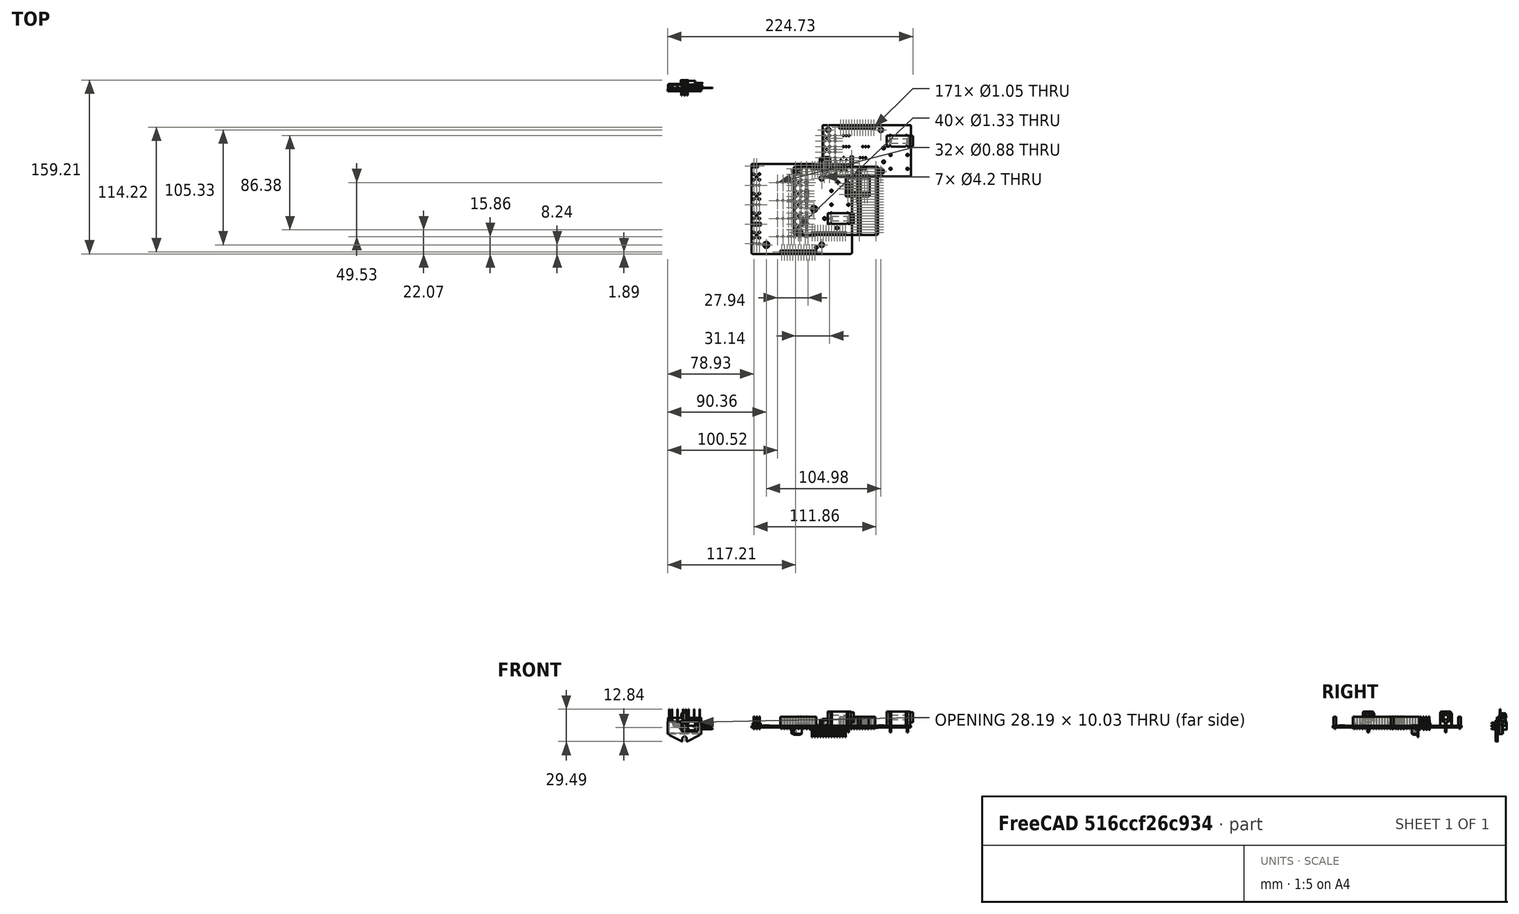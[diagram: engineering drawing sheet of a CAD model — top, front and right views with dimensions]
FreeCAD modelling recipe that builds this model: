
FCSTD DOCUMENT  (FreeCAD 1.1R20260108 (Git shallow))
Label: KiCadStepUp
License: All rights reserved
LicenseURL: https://en.wikipedia.org/wiki/All_rights_reserved
objects: Part::Feature×96, App::Link×57, App::Point×27, App::Part×27, PartDesign::CoordinateSystem×4, Sketcher::SketchObject×4
note: 108 computed .brp shape members not serialized (recipe doc carries the construction recipe); baked Part::Feature solids carry a one-line shape summary decoded from their .brp

FEATURE [App::Point] Origin028  label="Origin038"
  Role = Origin
FEATURE [PartDesign::CoordinateSystem] Local_CS_ba79
  AttacherType = Attacher::AttachEngine3D
  MapMode = 2
FEATURE [App::Point] Origin030
  Role = Origin
FEATURE [Part::Feature] Pcb_ba79
  shape: bbox 76.99 x 62.48 x 1.857 mm, 142 faces (baked)
FEATURE [Sketcher::SketchObject] PCB_Sketch_ba79
  ArcFitTolerance = 1e-06
  ExternalTypes = [0]
  FullyConstrained = false
  MakeInternals = false
  sketch-geometry (8):
    g0: LineSegment StartX=100.265 StartY=-130.75 StartZ=0 EndX=100.265 EndY=-70.27 EndZ=0
    g1: LineSegment StartX=176.25 StartY=-131.75 StartZ=0 EndX=101.265 EndY=-131.75 EndZ=0
    g2: LineSegment StartX=177.25 StartY=-70.27 StartZ=0 EndX=177.25 EndY=-130.75 EndZ=0
    g3: LineSegment StartX=101.265 StartY=-69.27 StartZ=0 EndX=176.25 EndY=-69.27 EndZ=0
    g4: ArcOfCircle CenterX=101.265 CenterY=-130.75 CenterZ=0 NormalX=0 NormalY=0 NormalZ=-1 AngleXU=-1.5708 Radius=0.999999 StartAngle=0 EndAngle=1.5708
    g5: ArcOfCircle CenterX=176.25 CenterY=-70.27 CenterZ=0 NormalX=0 NormalY=0 NormalZ=-1 AngleXU=1.5708 Radius=0.999999 StartAngle=0 EndAngle=1.5708
    g6: ArcOfCircle CenterX=176.25 CenterY=-130.75 CenterZ=0 NormalX=0 NormalY=0 NormalZ=-1 AngleXU=3.14159 Radius=0.999999 StartAngle=0 EndAngle=1.5708
    g7: ArcOfCircle CenterX=101.265 CenterY=-70.27 CenterZ=0 NormalX=0 NormalY=0 NormalZ=-1 AngleXU=-7.47076e-07 Radius=0.999999 StartAngle=0 EndAngle=1.5708
  constraints (8):
    c: Coincident(g0,g4)
    c: Coincident(g0,g7)
    c: Coincident(g1,g4)
    c: Coincident(g3,g7)
    c: Coincident(g1,g6)
    c: Coincident(g3,g5)
    c: Coincident(g2,g6)
    c: Coincident(g2,g5)
FEATURE [App::Part] Board_Geoms_ba79
  Group = -> [Pcb_ba79,PCB_Sketch_ba79]
  Origin = -> Origin031
FEATURE [App::Point] Origin032  label="Origin041"
  Role = Origin
FEATURE [App::Point] Origin034  label="Origin043"
  Role = Origin
FEATURE [Part::Feature] Shape005  label="J9_PinHeader_1x03_P254mm_Vertical_ad4b973e827e"
  Placement = pos=(111.86,-91.62,0) rot=(0,0,1;0rad)
  shape: bbox 2.54 x 7.62 x 11.54 mm, 76 faces (baked)
FEATURE [App::Link] J9_PinHeader_1x03_P254mm_Vertical_ad4b973e827e_ln_  label="J11_PinHeader_1x03_P254mm_Vertical_55ebcab31f16"
  LinkPlacement = pos=(111.86,-111.94,0) rot=(0,0,1;0rad)
  LinkedObject = -> Shape005
  Placement = pos=(111.86,-111.94,0) rot=(0,0,1;0rad)
FEATURE [App::Point] Origin036  label="Origin044"
  Role = Origin
FEATURE [Part::Feature] Part__Feature030  label="BODY-QFN"
  Placement = pos=(0,0,0.025) rot=(1,0,0;1.5708rad)
  shape: bbox 5 x 5 x 0.975 mm, 161 faces (baked)
FEATURE [App::Point] Origin038  label="Origin046"
  Role = Origin
FEATURE [Part::Feature] Part__Feature031  label="FRAME-RHB0032T"
  Placement = pos=(0,0,0) rot=(1,0,0;1.5708rad)
  shape: bbox 3.65 x 3.65 x 0.2 mm, 12 faces (baked)
FEATURE [Part::Feature] Part__Feature032  label="FRAME-RHB0032T001"
  Placement = pos=(0,0,0) rot=(1,0,0;1.5708rad)
  shape: bbox 0.4202 x 0.2502 x 0.2002 mm, 15 faces (baked)
FEATURE [Part::Feature] Part__Feature033  label="FRAME-RHB0032T002"
  Placement = pos=(0,0,0) rot=(1,0,0;1.5708rad)
  shape: bbox 0.4202 x 0.2502 x 0.2002 mm, 13 faces (baked)
FEATURE [Part::Feature] Part__Feature034  label="FRAME-RHB0032T003"
  Placement = pos=(0,0,0) rot=(1,0,0;1.5708rad)
  shape: bbox 0.4202 x 0.2502 x 0.2002 mm, 13 faces (baked)
FEATURE [Part::Feature] Part__Feature035  label="FRAME-RHB0032T004"
  Placement = pos=(0,0,0) rot=(1,0,0;1.5708rad)
  shape: bbox 0.4202 x 0.2502 x 0.2002 mm, 13 faces (baked)
FEATURE [Part::Feature] Part__Feature036  label="FRAME-RHB0032T005"
  Placement = pos=(0,0,0) rot=(1,0,0;1.5708rad)
  shape: bbox 0.4202 x 0.2502 x 0.2002 mm, 13 faces (baked)
FEATURE [Part::Feature] Part__Feature037  label="FRAME-RHB0032T006"
  Placement = pos=(0,0,0) rot=(1,0,0;1.5708rad)
  shape: bbox 0.4202 x 0.2502 x 0.2002 mm, 15 faces (baked)
FEATURE [Part::Feature] Part__Feature038  label="FRAME-RHB0032T007"
  Placement = pos=(0,0,0) rot=(1,0,0;1.5708rad)
  shape: bbox 0.4202 x 0.2502 x 0.2002 mm, 13 faces (baked)
FEATURE [Part::Feature] Part__Feature039  label="FRAME-RHB0032T008"
  Placement = pos=(0,0,0) rot=(1,0,0;1.5708rad)
  shape: bbox 0.4202 x 0.2502 x 0.2002 mm, 13 faces (baked)
FEATURE [Part::Feature] Part__Feature040  label="FRAME-RHB0032T009"
  Placement = pos=(0,0,0) rot=(1,0,0;1.5708rad)
  shape: bbox 0.4202 x 0.2502 x 0.2002 mm, 13 faces (baked)
FEATURE [Part::Feature] Part__Feature041  label="FRAME-RHB0032T010"
  Placement = pos=(0,0,0) rot=(1,0,0;1.5708rad)
  shape: bbox 0.4202 x 0.2502 x 0.2002 mm, 13 faces (baked)
FEATURE [Part::Feature] Part__Feature042  label="FRAME-RHB0032T011"
  Placement = pos=(0,0,0) rot=(1,0,0;1.5708rad)
  shape: bbox 0.4202 x 0.2502 x 0.2002 mm, 13 faces (baked)
FEATURE [Part::Feature] Part__Feature043  label="FRAME-RHB0032T012"
  Placement = pos=(0,0,0) rot=(1,0,0;1.5708rad)
  shape: bbox 0.4202 x 0.2502 x 0.2002 mm, 13 faces (baked)
FEATURE [Part::Feature] Part__Feature044  label="FRAME-RHB0032T013"
  Placement = pos=(0,0,0) rot=(1,0,0;1.5708rad)
  shape: bbox 0.4202 x 0.2502 x 0.2002 mm, 15 faces (baked)
FEATURE [Part::Feature] Part__Feature045  label="FRAME-RHB0032T014"
  Placement = pos=(0,0,0) rot=(1,0,0;1.5708rad)
  shape: bbox 0.4202 x 0.2502 x 0.2002 mm, 13 faces (baked)
FEATURE [Part::Feature] Part__Feature046  label="FRAME-RHB0032T015"
  Placement = pos=(0,0,0) rot=(1,0,0;1.5708rad)
  shape: bbox 0.4202 x 0.2502 x 0.2002 mm, 13 faces (baked)
FEATURE [Part::Feature] Part__Feature047  label="FRAME-RHB0032T016"
  Placement = pos=(0,0,0) rot=(1,0,0;1.5708rad)
  shape: bbox 0.4202 x 0.2502 x 0.2002 mm, 15 faces (baked)
FEATURE [Part::Feature] Part__Feature048  label="FRAME-RHB0032T017"
  Placement = pos=(0,0,0) rot=(1,0,0;1.5708rad)
  shape: bbox 0.2502 x 0.4202 x 0.2002 mm, 15 faces (baked)
FEATURE [Part::Feature] Part__Feature049  label="FRAME-RHB0032T018"
  Placement = pos=(0,0,0) rot=(1,0,0;1.5708rad)
  shape: bbox 0.2502 x 0.4202 x 0.2002 mm, 13 faces (baked)
FEATURE [Part::Feature] Part__Feature050  label="FRAME-RHB0032T019"
  Placement = pos=(0,0,0) rot=(1,0,0;1.5708rad)
  shape: bbox 0.2502 x 0.4202 x 0.2002 mm, 13 faces (baked)
FEATURE [Part::Feature] Part__Feature051  label="FRAME-RHB0032T020"
  Placement = pos=(0,0,0) rot=(1,0,0;1.5708rad)
  shape: bbox 0.2502 x 0.4202 x 0.2002 mm, 13 faces (baked)
FEATURE [Part::Feature] Part__Feature052  label="FRAME-RHB0032T021"
  Placement = pos=(0,0,0) rot=(1,0,0;1.5708rad)
  shape: bbox 0.2502 x 0.4202 x 0.2002 mm, 13 faces (baked)
FEATURE [Part::Feature] Part__Feature053  label="FRAME-RHB0032T022"
  Placement = pos=(0,0,0) rot=(1,0,0;1.5708rad)
  shape: bbox 0.2502 x 0.4202 x 0.2002 mm, 13 faces (baked)
FEATURE [Part::Feature] Part__Feature054  label="FRAME-RHB0032T023"
  Placement = pos=(0,0,0) rot=(1,0,0;1.5708rad)
  shape: bbox 0.2502 x 0.4202 x 0.2002 mm, 13 faces (baked)
FEATURE [Part::Feature] Part__Feature055  label="FRAME-RHB0032T024"
  Placement = pos=(0,0,0) rot=(1,0,0;1.5708rad)
  shape: bbox 0.2502 x 0.4202 x 0.2002 mm, 15 faces (baked)
FEATURE [Part::Feature] Part__Feature056  label="FRAME-RHB0032T025"
  Placement = pos=(0,0,0) rot=(1,0,0;1.5708rad)
  shape: bbox 0.2502 x 0.4202 x 0.2002 mm, 15 faces (baked)
FEATURE [Part::Feature] Part__Feature057  label="FRAME-RHB0032T026"
  Placement = pos=(0,0,0) rot=(1,0,0;1.5708rad)
  shape: bbox 0.2502 x 0.4202 x 0.2002 mm, 13 faces (baked)
FEATURE [Part::Feature] Part__Feature058  label="FRAME-RHB0032T027"
  Placement = pos=(0,0,0) rot=(1,0,0;1.5708rad)
  shape: bbox 0.2502 x 0.4202 x 0.2002 mm, 13 faces (baked)
FEATURE [Part::Feature] Part__Feature059  label="FRAME-RHB0032T028"
  Placement = pos=(0,0,0) rot=(1,0,0;1.5708rad)
  shape: bbox 0.2502 x 0.4202 x 0.2002 mm, 13 faces (baked)
FEATURE [Part::Feature] Part__Feature060  label="FRAME-RHB0032T029"
  Placement = pos=(0,0,0) rot=(1,0,0;1.5708rad)
  shape: bbox 0.2502 x 0.4202 x 0.2002 mm, 13 faces (baked)
FEATURE [Part::Feature] Part__Feature061  label="FRAME-RHB0032T030"
  Placement = pos=(0,0,0) rot=(1,0,0;1.5708rad)
  shape: bbox 0.2502 x 0.4202 x 0.2002 mm, 13 faces (baked)
FEATURE [Part::Feature] Part__Feature062  label="FRAME-RHB0032T031"
  Placement = pos=(0,0,0) rot=(1,0,0;1.5708rad)
  shape: bbox 0.2502 x 0.4202 x 0.2002 mm, 13 faces (baked)
FEATURE [Part::Feature] Part__Feature063  label="FRAME-RHB0032T032"
  Placement = pos=(0,0,0) rot=(1,0,0;1.5708rad)
  shape: bbox 0.2502 x 0.4202 x 0.2002 mm, 15 faces (baked)
FEATURE [App::Part] FRAME_RHB0032T  label="FRAME-RHB0032T033"
  Group = -> [Part__Feature031,Part__Feature032,Part__Feature033,Part__Feature034,Part__Feature035,Part__Feature036,Part__Feature037,Part__Feature038,Part__Feature039,Part__Feature040,Part__Feature041,Part__Feature042,Part__Feature043,Part__Feature044,Part__Feature045,Part__Feature046,Part__Feature047,Part__Feature048,Part__Feature049,Part__Feature050,Part__Feature051,Part__Feature052,Part__Feature053,+10 more]
  Origin = -> Origin039
FEATURE [App::Part] RHB0032T_ASM  label="U3_RHB0032T_ASM_5766224c6118"
  Group = -> [Part__Feature030,FRAME_RHB0032T]
  Origin = -> Origin037
  Placement = pos=(140.588,-83.69,0) rot=(0,0,1;0rad)
FEATURE [Part::Feature] Shape006  label="J16_PinSocket_1x24_P2.54mm_Vertical_78b5cde61121"
  Placement = pos=(160.12,-71.3,0) rot=(0,0,1;0rad)
  shape: bbox 2.54 x 60.96 x 11.6 mm, 634 faces (baked)
FEATURE [App::Link] J16_PinSocket_1x24_P2_54mm_Vertical_78b5cde61121_ln_  label="J19_PinSocket_1x24_P2.54mm_Vertical_494c607e0d7c"
  LinkPlacement = pos=(175.36,-129.72,0) rot=(0,0,1;3.14159rad)
  LinkedObject = -> Shape006
  Placement = pos=(175.36,-129.72,0) rot=(0,0,1;3.14159rad)
FEATURE [App::Link] J9_PinHeader_1x03_P254mm_Vertical_ad4b973e827e_ln_001  label="J12_PinHeader_1x03_P254mm_Vertical_f2afb972c277"
  LinkPlacement = pos=(111.86,-122.1,0) rot=(0,0,1;0rad)
  LinkedObject = -> Shape005
  Placement = pos=(111.86,-122.1,0) rot=(0,0,1;0rad)
FEATURE [Part::Feature] Shape007  label="J13_PinHeader_1x02_P254mm_Vertical_20b481d510b4"
  Placement = pos=(104.24,-129.72,0) rot=(0,0,1;1.5708rad)
  shape: bbox 5.08 x 2.54 x 11.54 mm, 52 faces (baked)
FEATURE [Part::Feature] Shape008  label="H1_24929_e929f093aded"
  Placement = pos=(118.64,-108.09,-1.5) rot=(1,0,0;1.5708rad)
  shape: bbox 5.564 x 5.564 x 1.848 mm, 14 faces (baked)
FEATURE [App::Link] J9_PinHeader_1x03_P254mm_Vertical_ad4b973e827e_ln_002  label="J7_PinHeader_1x03_P254mm_Vertical_729bbf1fc21d"
  LinkPlacement = pos=(111.86,-71.3,0) rot=(0,0,1;0rad)
  LinkedObject = -> Shape005
  Placement = pos=(111.86,-71.3,0) rot=(0,0,1;0rad)
FEATURE [App::Link] J9_PinHeader_1x03_P254mm_Vertical_ad4b973e827e_ln_003  label="J10_PinHeader_1x03_P254mm_Vertical_791fdefc0575"
  LinkPlacement = pos=(111.86,-101.78,0) rot=(0,0,1;0rad)
  LinkedObject = -> Shape005
  Placement = pos=(111.86,-101.78,0) rot=(0,0,1;0rad)
FEATURE [App::Link] J9_PinHeader_1x03_P254mm_Vertical_ad4b973e827e_ln_004  label="J8_PinHeader_1x03_P254mm_Vertical_44c2abdee4d8"
  LinkPlacement = pos=(111.86,-81.46,0) rot=(0,0,1;0rad)
  LinkedObject = -> Shape005
  Placement = pos=(111.86,-81.46,0) rot=(0,0,1;0rad)
FEATURE [App::Part] Top_ba79
  Group = -> [Shape005,J9_PinHeader_1x03_P254mm_Vertical_ad4b973e827e_ln_,RHB0032T_ASM,Shape006,J16_PinSocket_1x24_P2_54mm_Vertical_78b5cde61121_ln_,J9_PinHeader_1x03_P254mm_Vertical_ad4b973e827e_ln_001,Shape007,Shape008,J9_PinHeader_1x03_P254mm_Vertical_ad4b973e827e_ln_002,J9_PinHeader_1x03_P254mm_Vertical_ad4b973e827e_ln_003,J9_PinHeader_1x03_P254mm_Vertical_ad4b973e827e_ln_004]
  Origin = -> Origin035
FEATURE [App::Point] Origin009  label="Origin011"
  Role = Origin
FEATURE [Part::Feature] Shape009  label="J1_body_f7b675b30739"
  Placement = pos=(97.75,-73.84,-5.1572) rot=(0.57735,0.57735,-0.57735;4.18879rad)
  shape: bbox 9.53 x 6 x 10 mm, 123 faces (baked)
FEATURE [App::Link] J1_body_f7b675b30739_ln_  label="J4_body_518719d08dc4"
  LinkPlacement = pos=(97.75,-104.32,-5.1572) rot=(0.57735,0.57735,-0.57735;4.18879rad)
  LinkedObject = -> Shape009
  Placement = pos=(97.75,-104.32,-5.1572) rot=(0.57735,0.57735,-0.57735;4.18879rad)
FEATURE [App::Link] J1_body_f7b675b30739_ln_001  label="J6_body_2e244baf9bd4"
  LinkPlacement = pos=(97.75,-124.64,-5.1572) rot=(0.57735,0.57735,-0.57735;4.18879rad)
  LinkedObject = -> Shape009
  Placement = pos=(97.75,-124.64,-5.1572) rot=(0.57735,0.57735,-0.57735;4.18879rad)
FEATURE [Part::Feature] Shape010  label="J15_PinHeader_1x13_P254mm_Vertical_096e2f1177e8"
  Placement = pos=(116.94,-71.3,-1.8572) rot=(0.707107,-0.707107,0;3.14159rad)
  shape: bbox 33.02 x 2.54 x 11.54 mm, 316 faces (baked)
FEATURE [App::Link] J15_PinHeader_1x13_P254mm_Vertical_096e2f1177e8_ln_  label="J14_PinHeader_1x13_P254mm_Vertical_ac024b3e8be3"
  LinkPlacement = pos=(116.94,-129.72,-1.8572) rot=(0.707107,-0.707107,0;3.14159rad)
  LinkedObject = -> Shape010
  Placement = pos=(116.94,-129.72,-1.8572) rot=(0.707107,-0.707107,0;3.14159rad)
FEATURE [App::Link] J1_body_f7b675b30739_ln_002  label="J2_body_e8e3a7c5d442"
  LinkPlacement = pos=(97.75,-84,-5.1572) rot=(0.57735,0.57735,-0.57735;4.18879rad)
  LinkedObject = -> Shape009
  Placement = pos=(97.75,-84,-5.1572) rot=(0.57735,0.57735,-0.57735;4.18879rad)
FEATURE [App::Link] J1_body_f7b675b30739_ln_003  label="J5_body_1c366539b1e2"
  LinkPlacement = pos=(97.75,-114.48,-5.1572) rot=(0.57735,0.57735,-0.57735;4.18879rad)
  LinkedObject = -> Shape009
  Placement = pos=(97.75,-114.48,-5.1572) rot=(0.57735,0.57735,-0.57735;4.18879rad)
FEATURE [App::Link] J1_body_f7b675b30739_ln_004  label="J3_body_628205ab1372"
  LinkPlacement = pos=(97.75,-94.16,-5.1572) rot=(0.57735,0.57735,-0.57735;4.18879rad)
  LinkedObject = -> Shape009
  Placement = pos=(97.75,-94.16,-5.1572) rot=(0.57735,0.57735,-0.57735;4.18879rad)
FEATURE [App::Part] Bot_ba79
  Group = -> [Shape009,J1_body_f7b675b30739_ln_,J1_body_f7b675b30739_ln_001,Shape010,J15_PinHeader_1x13_P254mm_Vertical_096e2f1177e8_ln_,J1_body_f7b675b30739_ln_002,J1_body_f7b675b30739_ln_003,J1_body_f7b675b30739_ln_004]
  Origin = -> Origin008
FEATURE [App::Part] Step_Models_ba79
  Group = -> [Top_ba79,Bot_ba79]
  Origin = -> Origin033
FEATURE [App::Part] Board_ba79  label="MainBoard"
  Group = -> [Local_CS_ba79,Board_Geoms_ba79,Step_Models_ba79]
  Origin = -> Origin029
  Placement = pos=(-50,0,13.5) rot=(0,0,1;0rad)
FEATURE [App::Point] Origin040  label="Origin048"
  Role = Origin
FEATURE [PartDesign::CoordinateSystem] Local_CS_c31d
  AttacherType = Attacher::AttachEngine3D
  MapMode = 2
FEATURE [App::Point] Origin042  label="Origin050"
  Role = Origin
FEATURE [Part::Feature] Pcb_c31d
  shape: bbox 81.11 x 47.1 x 1.626 mm, 93 faces (baked)
FEATURE [Sketcher::SketchObject] PCB_Sketch_c31d
  ArcFitTolerance = 1e-06
  ExternalTypes = [0]
  FullyConstrained = false
  MakeInternals = false
  sketch-geometry (8):
    g0: LineSegment StartX=206.51 StartY=-78.31 StartZ=0 EndX=127.405 EndY=-78.31 EndZ=0
    g1: LineSegment StartX=207.51 StartY=-32.21 StartZ=0 EndX=207.51 EndY=-77.31 EndZ=0
    g2: LineSegment StartX=127.405 StartY=-31.21 StartZ=0 EndX=206.51 EndY=-31.21 EndZ=0
    g3: LineSegment StartX=126.405 StartY=-77.31 StartZ=0 EndX=126.405 EndY=-32.21 EndZ=0
    g4: ArcOfCircle CenterX=127.405 CenterY=-32.21 CenterZ=0 NormalX=0 NormalY=0 NormalZ=-1 AngleXU=-7.47076e-07 Radius=0.999999 StartAngle=0 EndAngle=1.5708
    g5: ArcOfCircle CenterX=206.51 CenterY=-32.21 CenterZ=0 NormalX=0 NormalY=0 NormalZ=-1 AngleXU=1.5708 Radius=0.999999 StartAngle=0 EndAngle=1.5708
    g6: ArcOfCircle CenterX=206.51 CenterY=-77.31 CenterZ=0 NormalX=0 NormalY=0 NormalZ=-1 AngleXU=3.14159 Radius=0.999999 StartAngle=0 EndAngle=1.5708
    g7: ArcOfCircle CenterX=127.405 CenterY=-77.31 CenterZ=0 NormalX=0 NormalY=0 NormalZ=-1 AngleXU=-1.5708 Radius=0.999999 StartAngle=0 EndAngle=1.5708
  constraints (8):
    c: Coincident(g3,g7)
    c: Coincident(g3,g4)
    c: Coincident(g0,g7)
    c: Coincident(g2,g4)
    c: Coincident(g0,g6)
    c: Coincident(g2,g5)
    c: Coincident(g1,g6)
    c: Coincident(g1,g5)
FEATURE [App::Part] Board_Geoms_c31d
  Group = -> [Pcb_c31d,PCB_Sketch_c31d]
  Origin = -> Origin043
FEATURE [App::Point] Origin044  label="Origin052"
  Role = Origin
FEATURE [App::Point] Origin046  label="Origin054"
  Role = Origin
FEATURE [Part::Feature] Shape011  label="J14_24.243.1_e307b03fb0da"
  Placement = pos=(204.3,-45.8,0) rot=(0,0,1;1.5708rad)
  shape: bbox 24 x 10.7 x 19 mm, 54 faces (baked)
FEATURE [App::Point] Origin048  label="Origin056"
  Role = Origin
FEATURE [Part::Feature] Part__Feature064  label="T03B_BODY"
  shape: bbox 8.636 x 4.572 x 10.16 mm, 21 faces (baked)
FEATURE [Part::Feature] Part__Feature065  label="T03B_LEAD"
  Placement = pos=(12.192,2.667,2.54) rot=(0,0,1;0rad)
  shape: bbox 13.72 x 0.381 x 1.27 mm, 12 faces (baked)
FEATURE [Part::Feature] Part__Feature066  label="T03B_LEAD001"
  Placement = pos=(12.192,2.667,0) rot=(0,0,1;0rad)
  shape: bbox 13.72 x 0.381 x 1.27 mm, 12 faces (baked)
FEATURE [Part::Feature] Part__Feature067  label="T03B_LEAD002"
  Placement = pos=(12.192,2.667,-2.54) rot=(0,0,1;0rad)
  shape: bbox 13.72 x 0.381 x 1.27 mm, 12 faces (baked)
FEATURE [Part::Feature] Part__Feature068  label="T03B_HS"
  Placement = pos=(0,0,0) rot=(0,1,0;1.5708rad)
  shape: bbox 12.4 x 1.27 x 10.16 mm, 16 faces (baked)
FEATURE [App::Part] T03B_ASM  label="U5_T03B_ASM_8a3d5432edab"
  Group = -> [Part__Feature064,Part__Feature065,Part__Feature066,Part__Feature067,Part__Feature068]
  Origin = -> Origin049
  Placement = pos=(163.4,-74.05,15.9) rot=(0,1,0;1.5708rad)
FEATURE [Part::Feature] Shape012  label="J3_body_2f07c1956b23"
  Placement = pos=(123.89,-63.58,3.3) rot=(0.57735,-0.57735,-0.57735;2.0944rad)
  shape: bbox 9.53 x 6 x 10 mm, 123 faces (baked)
FEATURE [App::Link] J14_24_243_1_e307b03fb0da_ln_  label="J13_24.243.1_6468255164de"
  LinkPlacement = pos=(204.3,-58.5,0) rot=(0,0,1;1.5708rad)
  LinkedObject = -> Shape011
  Placement = pos=(204.3,-58.5,0) rot=(0,0,1;1.5708rad)
FEATURE [Part::Feature] Shape013  label="J7_PinHeader_1x03_P254mm_Vertical_d4164e279ff0"
  Placement = pos=(153.24,-61.04,0) rot=(0,0,1;0rad)
  shape: bbox 2.54 x 7.62 x 11.54 mm, 76 faces (baked)
FEATURE [Part::Feature] Shape014  label="H4_24929_250e951c427d"
  Placement = pos=(179.91,-73.74,-1.5) rot=(1,0,0;1.5708rad)
  shape: bbox 5.564 x 5.564 x 1.848 mm, 14 faces (baked)
FEATURE [App::Link] J7_PinHeader_1x03_P254mm_Vertical_d4164e279ff0_ln_  label="J8_PinHeader_1x03_P254mm_Vertical_56ebdcdbe8a9"
  LinkPlacement = pos=(153.24,-71.2,0) rot=(0,0,1;0rad)
  LinkedObject = -> Shape013
  Placement = pos=(153.24,-71.2,0) rot=(0,0,1;0rad)
FEATURE [App::Link] J7_PinHeader_1x03_P254mm_Vertical_d4164e279ff0_ln_001  label="J5_PinHeader_1x03_P254mm_Vertical_7514f616a686"
  LinkPlacement = pos=(138,-40.72,0) rot=(0,0,1;0rad)
  LinkedObject = -> Shape013
  Placement = pos=(138,-40.72,0) rot=(0,0,1;0rad)
FEATURE [App::Link] U5_T03B_ASM_8a3d5432edab_ln_  label="U2_T03B_ASM_e99f09d6277a"
  LinkPlacement = pos=(165.94,-53.73,15.9) rot=(0,1,0;1.5708rad)
  LinkedObject = -> T03B_ASM
  Placement = pos=(165.94,-53.73,15.9) rot=(0,1,0;1.5708rad)
FEATURE [App::Link] J7_PinHeader_1x03_P254mm_Vertical_d4164e279ff0_ln_002  label="J10_PinHeader_1x03_P254mm_Vertical_8da6b36ed773"
  LinkPlacement = pos=(138,-71.2,0) rot=(0,0,1;0rad)
  LinkedObject = -> Shape013
  Placement = pos=(138,-71.2,0) rot=(0,0,1;0rad)
FEATURE [App::Link] H4_24929_250e951c427d_ln_  label="H1_24929_3b742a38075a"
  LinkPlacement = pos=(131.65,-35.64,-1.5) rot=(1,0,0;1.5708rad)
  LinkedObject = -> Shape014
  Placement = pos=(131.65,-35.64,-1.5) rot=(1,0,0;1.5708rad)
FEATURE [App::Link] J3_body_2f07c1956b23_ln_  label="J4_body_0bb9c7696e41"
  LinkPlacement = pos=(123.89,-73.74,3.3) rot=(0.57735,-0.57735,-0.57735;2.0944rad)
  LinkedObject = -> Shape012
  Placement = pos=(123.89,-73.74,3.3) rot=(0.57735,-0.57735,-0.57735;2.0944rad)
FEATURE [App::Link] J7_PinHeader_1x03_P254mm_Vertical_d4164e279ff0_ln_003  label="J9_PinHeader_1x03_P254mm_Vertical_9506bcbbbcae"
  LinkPlacement = pos=(138,-61.04,0) rot=(0,0,1;0rad)
  LinkedObject = -> Shape013
  Placement = pos=(138,-61.04,0) rot=(0,0,1;0rad)
FEATURE [App::Link] U5_T03B_ASM_8a3d5432edab_ln_001  label="U6_T03B_ASM_9871e3979828"
  LinkPlacement = pos=(163.4,-63.89,15.9) rot=(0,1,0;1.5708rad)
  LinkedObject = -> T03B_ASM
  Placement = pos=(163.4,-63.89,15.9) rot=(0,1,0;1.5708rad)
FEATURE [Part::Feature] Shape015  label="J11_PinSocket_1x13_P2.54mm_Vertical_dffe24c4024b"
  Placement = pos=(143.08,-33.1,0) rot=(0,0,1;1.5708rad)
  shape: bbox 33.02 x 2.54 x 11.6 mm, 348 faces (baked)
FEATURE [App::Link] H4_24929_250e951c427d_ln_001  label="H2_24929_a5312c11b352"
  LinkPlacement = pos=(179.91,-35.64,-1.5) rot=(1,0,0;1.5708rad)
  LinkedObject = -> Shape014
  Placement = pos=(179.91,-35.64,-1.5) rot=(1,0,0;1.5708rad)
FEATURE [App::Link] J7_PinHeader_1x03_P254mm_Vertical_d4164e279ff0_ln_004  label="J6_PinHeader_1x03_P254mm_Vertical_bd20f2f1355f"
  LinkPlacement = pos=(138,-50.88,0) rot=(0,0,1;0rad)
  LinkedObject = -> Shape013
  Placement = pos=(138,-50.88,0) rot=(0,0,1;0rad)
FEATURE [App::Link] J14_24_243_1_e307b03fb0da_ln_001  label="J12_24.243.1_666f44d342c5"
  LinkPlacement = pos=(204.3,-71.2,0) rot=(0,0,1;1.5708rad)
  LinkedObject = -> Shape011
  Placement = pos=(204.3,-71.2,0) rot=(0,0,1;1.5708rad)
FEATURE [App::Link] J3_body_2f07c1956b23_ln_001  label="J2_body_f47d0df4af63"
  LinkPlacement = pos=(123.89,-53.42,3.3) rot=(0.57735,-0.57735,-0.57735;2.0944rad)
  LinkedObject = -> Shape012
  Placement = pos=(123.89,-53.42,3.3) rot=(0.57735,-0.57735,-0.57735;2.0944rad)
FEATURE [App::Point] Origin050  label="Origin058"
  Role = Origin
FEATURE [Part::Feature] Part__Feature069  label="3296Y-1-102LF"
  shape: bbox 10.03 x 9.53 x 4.83 mm, 20 faces (baked)
FEATURE [Part::Feature] Part__Feature070  label="3296Y-1-102LF001"
  shape: bbox 1.52 x 2.19 x 2.19 mm, 8 faces (baked)
FEATURE [Part::Feature] Part__Feature071  label="3296Y-1-102LF002"
  shape: bbox 6.78 x 0.51 x 0.51 mm, 4 faces (baked)
FEATURE [Part::Feature] Part__Feature072  label="3296Y-1-102LF003"
  shape: bbox 6.78 x 0.51 x 0.51 mm, 4 faces (baked)
FEATURE [Part::Feature] Part__Feature073  label="3296Y-1-102LF004"
  shape: bbox 6.78 x 0.51 x 0.51 mm, 4 faces (baked)
FEATURE [App::Part] _3296Y_1_102LF  label="RV2_3296Y-1-102LF005_d061cea9672d"
  Group = -> [Part__Feature069,Part__Feature070,Part__Feature071,Part__Feature072,Part__Feature073]
  Origin = -> Origin051
  Placement = pos=(141.01,-59.48,10) rot=(0.57735,0.57735,-0.57735;2.0944rad)
FEATURE [App::Link] U5_T03B_ASM_8a3d5432edab_ln_002  label="U1_T03B_ASM_e9f2a18246d3"
  LinkPlacement = pos=(148.16,-53.73,15.9) rot=(0,1,0;1.5708rad)
  LinkedObject = -> T03B_ASM
  Placement = pos=(148.16,-53.73,15.9) rot=(0,1,0;1.5708rad)
FEATURE [App::Link] RV2_3296Y_1_102LF005_d061cea9672d_ln_  label="RV1_3296Y-1-102LF005_1b39bf32728c"
  LinkPlacement = pos=(141.01,-69.64,10) rot=(0.57735,0.57735,-0.57735;2.0944rad)
  LinkedObject = -> _3296Y_1_102LF
  Placement = pos=(141.01,-69.64,10) rot=(0.57735,0.57735,-0.57735;2.0944rad)
FEATURE [App::Link] J3_body_2f07c1956b23_ln_002  label="J1_body_b5292fdc43ba"
  LinkPlacement = pos=(123.89,-43.26,3.3) rot=(0.57735,-0.57735,-0.57735;2.0944rad)
  LinkedObject = -> Shape012
  Placement = pos=(123.89,-43.26,3.3) rot=(0.57735,-0.57735,-0.57735;2.0944rad)
FEATURE [App::Link] U5_T03B_ASM_8a3d5432edab_ln_003  label="U3_T03B_ASM_9718203a4af7"
  LinkPlacement = pos=(148.16,-43.57,15.9) rot=(0,1,0;1.5708rad)
  LinkedObject = -> T03B_ASM
  Placement = pos=(148.16,-43.57,15.9) rot=(0,1,0;1.5708rad)
FEATURE [App::Part] Top_c31d
  Group = -> [Shape011,T03B_ASM,Shape012,J14_24_243_1_e307b03fb0da_ln_,Shape013,Shape014,J7_PinHeader_1x03_P254mm_Vertical_d4164e279ff0_ln_,J7_PinHeader_1x03_P254mm_Vertical_d4164e279ff0_ln_001,U5_T03B_ASM_8a3d5432edab_ln_,J7_PinHeader_1x03_P254mm_Vertical_d4164e279ff0_ln_002,H4_24929_250e951c427d_ln_,J3_body_2f07c1956b23_ln_,J7_PinHeader_1x03_P254mm_Vertical_d4164e279ff0_ln_003,U5_T03B_ASM_8a3d5432edab_ln_001,+10 more]
  Origin = -> Origin047
FEATURE [App::Part] Step_Models_c31d
  Group = -> [Top_c31d]
  Origin = -> Origin045
FEATURE [App::Part] Board_c31d  label="PowerBoard"
  Group = -> [Local_CS_c31d,Board_Geoms_c31d,Step_Models_c31d]
  Origin = -> Origin041
  Placement = pos=(-76,-96.5,0) rot=(0,0,1;0rad)
FEATURE [App::Point] Origin052  label="Origin060"
  Role = Origin
FEATURE [PartDesign::CoordinateSystem] Local_CS_2479
  AttacherType = Attacher::AttachEngine3D
  MapMode = 2
FEATURE [App::Point] Origin054  label="Origin062"
  Role = Origin
FEATURE [Part::Feature] Pcb_2479
  shape: bbox 21.84 x 19.02 x 1.626 mm, 29 faces (baked)
FEATURE [Sketcher::SketchObject] PCB_Sketch_2479
  ArcFitTolerance = 1e-06
  ExternalTypes = [0]
  FullyConstrained = false
  MakeInternals = false
  sketch-geometry (8):
    g0: LineSegment StartX=147.78 StartY=-95.74 StartZ=0 EndX=147.78 EndY=-78.72 EndZ=0
    g1: LineSegment StartX=168.62 StartY=-96.74 StartZ=0 EndX=148.78 EndY=-96.74 EndZ=0
    g2: LineSegment StartX=169.62 StartY=-78.72 StartZ=0 EndX=169.62 EndY=-95.74 EndZ=0
    g3: LineSegment StartX=148.78 StartY=-77.72 StartZ=0 EndX=168.62 EndY=-77.72 EndZ=0
    g4: ArcOfCircle CenterX=168.62 CenterY=-95.74 CenterZ=0 NormalX=0 NormalY=0 NormalZ=-1 AngleXU=3.14159 Radius=0.999999 StartAngle=0 EndAngle=1.5708
    g5: ArcOfCircle CenterX=168.62 CenterY=-78.72 CenterZ=0 NormalX=0 NormalY=0 NormalZ=-1 AngleXU=1.5708 Radius=0.999999 StartAngle=0 EndAngle=1.5708
    g6: ArcOfCircle CenterX=148.78 CenterY=-78.72 CenterZ=0 NormalX=0 NormalY=0 NormalZ=-1 AngleXU=-7.47076e-07 Radius=0.999999 StartAngle=0 EndAngle=1.5708
    g7: ArcOfCircle CenterX=148.78 CenterY=-95.74 CenterZ=0 NormalX=0 NormalY=0 NormalZ=-1 AngleXU=-1.5708 Radius=0.999999 StartAngle=0 EndAngle=1.5708
  constraints (8):
    c: Coincident(g0,g7)
    c: Coincident(g0,g6)
    c: Coincident(g1,g7)
    c: Coincident(g3,g6)
    c: Coincident(g1,g4)
    c: Coincident(g3,g5)
    c: Coincident(g2,g4)
    c: Coincident(g2,g5)
FEATURE [App::Part] Board_Geoms_2479
  Group = -> [Pcb_2479,PCB_Sketch_2479]
  Origin = -> Origin055
FEATURE [App::Point] Origin056  label="Origin064"
  Role = Origin
FEATURE [App::Point] Origin058  label="Origin066"
  Role = Origin
FEATURE [Part::Feature] Shape016  label="J3_PinSocket_1x08_P2.54mm_Vertical_5b6a1543d123"
  Placement = pos=(149.81,-94.85,0) rot=(0,0,1;1.5708rad)
  shape: bbox 20.32 x 2.54 x 11.6 mm, 218 faces (baked)
FEATURE [App::Link] J3_PinSocket_1x08_P2_54mm_Vertical_5b6a1543d123_ln_  label="J2_PinSocket_1x08_P2.54mm_Vertical_80ce480c65d9"
  LinkPlacement = pos=(149.81,-79.61,0) rot=(0,0,1;1.5708rad)
  LinkedObject = -> Shape016
  Placement = pos=(149.81,-79.61,0) rot=(0,0,1;1.5708rad)
FEATURE [Part::Feature] Shape017  label="J1_PinHeader_1x03_P254mm_Vertical_4f288b3d8411"
  Placement = pos=(149.81,-84.69,0) rot=(0,0,1;0rad)
  shape: bbox 2.54 x 7.62 x 11.54 mm, 76 faces (baked)
FEATURE [App::Part] Top_2479
  Group = -> [Shape016,J3_PinSocket_1x08_P2_54mm_Vertical_5b6a1543d123_ln_,Shape017]
  Origin = -> Origin059
FEATURE [App::Part] Step_Models_2479
  Group = -> [Top_2479]
  Origin = -> Origin057
FEATURE [App::Part] Board_2479  label="TIA1"
  Group = -> [Local_CS_2479,Board_Geoms_2479,Step_Models_2479]
  Origin = -> Origin053
  Placement = pos=(90,60,0) rot=(0,0,1;-1.5708rad)
FEATURE [App::Point] Origin003
  Role = Origin
FEATURE [PartDesign::CoordinateSystem] Local_CS_4ccb
  AttacherType = Attacher::AttachEngine3D
  MapMode = 2
FEATURE [App::Point] Origin001
  Role = Origin
FEATURE [Part::Feature] Pcb_4ccb
  shape: bbox 91.86 x 82.52 x 1.626 mm, 100 faces (baked)
FEATURE [Sketcher::SketchObject] PCB_Sketch_4ccb
  ArcFitTolerance = 1e-06
  ExternalTypes = [0]
  FullyConstrained = false
  MakeInternals = false
  sketch-geometry (8):
    g0: LineSegment StartX=61.47 StartY=-148.21 StartZ=0 EndX=61.47 EndY=-67.69 EndZ=0
    g1: LineSegment StartX=62.47 StartY=-66.69 StartZ=0 EndX=152.33 EndY=-66.69 EndZ=0
    g2: LineSegment StartX=153.33 StartY=-67.69 StartZ=0 EndX=153.33 EndY=-148.21 EndZ=0
    g3: LineSegment StartX=152.33 StartY=-149.21 StartZ=0 EndX=62.47 EndY=-149.21 EndZ=0
    g4: ArcOfCircle CenterX=152.33 CenterY=-67.69 CenterZ=0 NormalX=0 NormalY=0 NormalZ=-1 AngleXU=1.5708 Radius=0.999999 StartAngle=0 EndAngle=1.5708
    g5: ArcOfCircle CenterX=152.33 CenterY=-148.21 CenterZ=0 NormalX=0 NormalY=0 NormalZ=-1 AngleXU=3.14159 Radius=0.999999 StartAngle=0 EndAngle=1.5708
    g6: ArcOfCircle CenterX=62.47 CenterY=-67.69 CenterZ=0 NormalX=0 NormalY=0 NormalZ=-1 AngleXU=-7.47076e-07 Radius=0.999999 StartAngle=0 EndAngle=1.5708
    g7: ArcOfCircle CenterX=62.47 CenterY=-148.21 CenterZ=0 NormalX=0 NormalY=0 NormalZ=-1 AngleXU=-1.5708 Radius=0.999999 StartAngle=0 EndAngle=1.5708
  constraints (8):
    c: Coincident(g0,g7)
    c: Coincident(g0,g6)
    c: Coincident(g3,g7)
    c: Coincident(g1,g6)
    c: Coincident(g3,g5)
    c: Coincident(g1,g4)
    c: Coincident(g2,g5)
    c: Coincident(g2,g4)
FEATURE [App::Part] Board_Geoms_4ccb
  Group = -> [Pcb_4ccb,PCB_Sketch_4ccb]
  Origin = -> Origin
FEATURE [App::Point] Origin005  label="Origin006"
  Role = Origin
FEATURE [App::Point] Origin007  label="Origin009"
  Role = Origin
FEATURE [App::Point] Origin017  label="Origin022"
  Role = Origin
FEATURE [Part::Feature] Part__Feature  label="PHM31"
  shape: bbox 30.86 x 1.854 x 18.36 mm, 20 faces (baked)
FEATURE [Part::Feature] Part__Feature001  label="PSB14"
  Placement = pos=(-4.8e-15,1.8542,9e-16) rot=(0,0,1;0rad)
  shape: bbox 30.48 x 1.016 x 14.99 mm, 6 faces (baked)
FEATURE [Part::Feature] Part__Feature002  label="PCP02F"
  Placement = pos=(-4e-16,4.4577,-1.4605) rot=(0,0,1;0rad)
  shape: bbox 30.23 x 3.175 x 12.07 mm, 27 faces (baked)
FEATURE [Part::Feature] Part__Feature003  label="PCP02L"
  Placement = pos=(-4e-16,5.7277,-1.4605) rot=(0,0,1;0rad)
  shape: bbox 29.62 x 1.524 x 11.46 mm, 69 faces (baked)
FEATURE [Part::Feature] Part__Feature004  label="PIN05_DQ"
  Placement = pos=(-13.97,4.1402,18.3388) rot=(0,-1,0;1.5708rad)
  shape: bbox 1.27 x 3.294 x 10.54 mm, 68 faces (baked)
FEATURE [Part::Feature] Part__Feature005  label="PIN05_DQ001"
  Placement = pos=(-11.43,4.1402,18.3388) rot=(0,-1,0;1.5708rad)
  shape: bbox 1.27 x 3.294 x 10.54 mm, 68 faces (baked)
FEATURE [Part::Feature] Part__Feature006  label="PIN05_DQ002"
  Placement = pos=(-6.35,4.1402,18.3388) rot=(0,-1,0;1.5708rad)
  shape: bbox 1.27 x 3.294 x 10.54 mm, 68 faces (baked)
FEATURE [Part::Feature] Part__Feature007  label="PIN05_DQ003"
  Placement = pos=(-1.27,4.1402,18.3388) rot=(0,-1,0;1.5708rad)
  shape: bbox 1.27 x 3.294 x 10.54 mm, 68 faces (baked)
FEATURE [Part::Feature] Part__Feature008  label="PIN05_DQ004"
  Placement = pos=(1.27,4.1402,18.3388) rot=(0,-1,0;1.5708rad)
  shape: bbox 1.27 x 3.294 x 10.54 mm, 68 faces (baked)
FEATURE [Part::Feature] Part__Feature009  label="PIN05_DQ005"
  Placement = pos=(3.81,4.1402,18.3388) rot=(0,-1,0;1.5708rad)
  shape: bbox 1.27 x 3.294 x 10.54 mm, 68 faces (baked)
FEATURE [Part::Feature] Part__Feature010  label="PIN05_DQ006"
  Placement = pos=(8.89,4.1402,18.3388) rot=(0,-1,0;1.5708rad)
  shape: bbox 1.27 x 3.294 x 10.54 mm, 68 faces (baked)
FEATURE [Part::Feature] Part__Feature011  label="PIN05_DQ007"
  Placement = pos=(13.97,4.1402,18.3388) rot=(0,-1,0;1.5708rad)
  shape: bbox 1.27 x 3.294 x 10.54 mm, 68 faces (baked)
FEATURE [App::Part] DQ  label="U3_DQ_af74b2632c74"
  Group = -> [Part__Feature,Part__Feature001,Part__Feature002,Part__Feature003,Part__Feature004,Part__Feature005,Part__Feature006,Part__Feature007,Part__Feature008,Part__Feature009,Part__Feature010,Part__Feature011]
  Origin = -> Origin016
  Placement = pos=(99.06,-104.23,8) rot=(0,1,0;3.14159rad)
FEATURE [App::Link] U3_DQ_af74b2632c74_ln_  label="U2_DQ_e1886966fc8a"
  LinkPlacement = pos=(99.06,-120.74,8) rot=(0,1,0;3.14159rad)
  LinkedObject = -> DQ
  Placement = pos=(99.06,-120.74,8) rot=(0,1,0;3.14159rad)
FEATURE [App::Point] Origin019  label="Origin025"
  Role = Origin
FEATURE [Part::Feature] Part__Feature012  label="GC355DD7LP474KX18K"
  shape: bbox 0.3 x 2 x 5 mm, 18 faces (baked)
FEATURE [Part::Feature] Part__Feature013  label="GC355DD7LP474KX18K001"
  shape: bbox 0.3 x 2 x 5 mm, 18 faces (baked)
FEATURE [Part::Feature] Part__Feature014  label="GC355DD7LP474KX18K002"
  shape: bbox 5.1 x 1.905 x 4.905 mm, 10 faces (baked)
FEATURE [App::Part] GC355DD7LP474KX18K  label="C11_GC355DD7LP474KX18K003_3832eaa5f01c"
  Group = -> [Part__Feature012,Part__Feature013,Part__Feature014]
  Origin = -> Origin018
  Placement = pos=(87.63,-77.089,0) rot=(1,0,0;1.5708rad)
FEATURE [Part::Feature] Shape  label="J10_PinHeader_1x03_P254mm_Vertical_3c94ed9524f8"
  Placement = pos=(63.5,-121.92,0) rot=(0,0,1;1.5708rad)
  shape: bbox 7.62 x 2.54 x 11.54 mm, 76 faces (baked)
FEATURE [App::Link] C11_GC355DD7LP474KX18K003_3832eaa5f01c_ln_  label="C1_GC355DD7LP474KX18K003_49afdd26f161"
  LinkPlacement = pos=(79.121,-130.556,0) rot=(0.57735,0.57735,0.57735;2.0944rad)
  LinkedObject = -> GC355DD7LP474KX18K
  Placement = pos=(79.121,-130.556,0) rot=(0.57735,0.57735,0.57735;2.0944rad)
FEATURE [App::Point] Origin021  label="Origin028"
  Role = Origin
FEATURE [Part::Feature] Part__Feature015  label="part"
  shape: bbox 1.778 x 2.516 x 0.688 mm, 6 faces (baked)
FEATURE [Part::Feature] Part__Feature016  label="part001"
  shape: bbox 0.762 x 2.59 x 0.762 mm, 6 faces (baked)
FEATURE [Part::Feature] Part__Feature017  label="part002"
  shape: bbox 0.762 x 2.59 x 0.762 mm, 6 faces (baked)
FEATURE [App::Part] part  label="R4_part003_2be0b62ebf49"
  Group = -> [Part__Feature015,Part__Feature016,Part__Feature017]
  Origin = -> Origin020
  Placement = pos=(106.426,-123.571,0) rot=(0,0,1;3.14159rad)
FEATURE [App::Link] R4_part003_2be0b62ebf49_ln_  label="R7_part003_68c99f16b766"
  LinkPlacement = pos=(106.426,-107.061,0) rot=(0,0,1;3.14159rad)
  LinkedObject = -> part
  Placement = pos=(106.426,-107.061,0) rot=(0,0,1;3.14159rad)
FEATURE [App::Link] J10_PinHeader_1x03_P254mm_Vertical_3c94ed9524f8_ln_  label="J7_PinHeader_1x03_P254mm_Vertical_2498897243b0"
  LinkPlacement = pos=(63.5,-139.7,0) rot=(0,0,1;1.5708rad)
  LinkedObject = -> Shape
  Placement = pos=(63.5,-139.7,0) rot=(0,0,1;1.5708rad)
FEATURE [Part::Feature] Shape001  label="H2_24929_41eebdcc3b95"
  Placement = pos=(74.93,-140.97,-1.5) rot=(1,0,0;1.5708rad)
  shape: bbox 5.564 x 5.564 x 1.848 mm, 14 faces (baked)
FEATURE [App::Point] Origin023  label="Origin031"
  Role = Origin
FEATURE [Part::Feature] Part__Feature018  label="RFPC-SMA27-F"
  shape: bbox 5.08 x 1.3 x 5.08 mm, 6 faces (baked)
FEATURE [Part::Feature] Part__Feature019  label="RFPC-SMA27-F001"
  shape: bbox 1.27 x 5.6 x 1.27 mm, 6 faces (baked)
FEATURE [Part::Feature] Part__Feature020  label="RFPC-SMA27-F002"
  shape: bbox 11.06 x 14.07 x 17.13 mm, 73 faces (baked)
FEATURE [Part::Feature] Part__Feature021  label="RFPC-SMA27-F003"
  shape: bbox 4.5 x 4.5 x 6.2 mm, 6 faces (baked)
FEATURE [Part::Feature] Part__Feature022  label="RFPC-SMA27-F004"
  shape: bbox 1.27 x 1.27 x 6.2 mm, 6 faces (baked)
FEATURE [App::Part] RFPC_SMA27_F  label="J6_RFPC-SMA27-F005_71e1e65d45ac"
  Group = -> [Part__Feature018,Part__Feature019,Part__Feature020,Part__Feature021,Part__Feature022]
  Origin = -> Origin022
  Placement = pos=(66.04,-132.08,0) rot=(0.57735,-0.57735,-0.57735;2.0944rad)
FEATURE [App::Link] R4_part003_2be0b62ebf49_ln_001  label="R10_part003_cfb6eb38ff5a"
  LinkPlacement = pos=(106.426,-90.551,0) rot=(0,0,1;3.14159rad)
  LinkedObject = -> part
  Placement = pos=(106.426,-90.551,0) rot=(0,0,1;3.14159rad)
FEATURE [App::Point] Origin025  label="Origin033"
  Role = Origin
FEATURE [Part::Feature] Part__Feature023  label="part003"
  shape: bbox 2.896 x 1.704 x 1.703 mm, 6 faces (baked)
FEATURE [Part::Feature] Part__Feature024  label="part004"
  shape: bbox 0.305 x 1.804 x 1.803 mm, 6 faces (baked)
FEATURE [Part::Feature] Part__Feature025  label="part005"
  shape: bbox 0.305 x 1.804 x 1.803 mm, 6 faces (baked)
FEATURE [Part::Feature] Part__Feature026  label="part006"
  shape: bbox 0.2899 x 1.709 x 1.709 mm, 12 faces (baked)
FEATURE [App::Part] part001  label="C6_part007_186ecd920058"
  Group = -> [Part__Feature023,Part__Feature024,Part__Feature025,Part__Feature026]
  Origin = -> Origin024
  Placement = pos=(102.87,-112.141,0) rot=(0,0,1;3.14159rad)
FEATURE [App::Link] J6_RFPC_SMA27_F005_71e1e65d45ac_ln_  label="J9_RFPC-SMA27-F005_6ae669eccaba"
  LinkPlacement = pos=(66.04,-114.3,0) rot=(0.57735,-0.57735,-0.57735;2.0944rad)
  LinkedObject = -> RFPC_SMA27_F
  Placement = pos=(66.04,-114.3,0) rot=(0.57735,-0.57735,-0.57735;2.0944rad)
FEATURE [App::Link] C11_GC355DD7LP474KX18K003_3832eaa5f01c_ln_001  label="C2_GC355DD7LP474KX18K003_6b9566a23919"
  LinkPlacement = pos=(87.63,-126.619,0) rot=(1,0,0;1.5708rad)
  LinkedObject = -> GC355DD7LP474KX18K
  Placement = pos=(87.63,-126.619,0) rot=(1,0,0;1.5708rad)
FEATURE [Part::Feature] Shape002  label="J3_24.243.1_edf6e0b226a5"
  Placement = pos=(150.12,-116.84,0) rot=(0,0,1;1.5708rad)
  shape: bbox 24 x 10.7 x 19 mm, 54 faces (baked)
FEATURE [App::Link] C6_part007_186ecd920058_ln_  label="C12_part007_330eeb041ce6"
  LinkPlacement = pos=(102.87,-79.121,0) rot=(0,0,1;3.14159rad)
  LinkedObject = -> part001
  Placement = pos=(102.87,-79.121,0) rot=(0,0,1;3.14159rad)
FEATURE [App::Link] H2_24929_41eebdcc3b95_ln_  label="H1_24929_fef8cef73cda"
  LinkPlacement = pos=(125.73,-80.01,-1.5) rot=(1,0,0;1.5708rad)
  LinkedObject = -> Shape001
  Placement = pos=(125.73,-80.01,-1.5) rot=(1,0,0;1.5708rad)
FEATURE [App::Link] R4_part003_2be0b62ebf49_ln_002  label="R13_part007_a1a74aec2e3f"
  LinkPlacement = pos=(106.426,-74.041,0) rot=(0,0,1;3.14159rad)
  LinkedObject = -> part
  Placement = pos=(106.426,-74.041,0) rot=(0,0,1;3.14159rad)
FEATURE [App::Link] J3_24_243_1_edf6e0b226a5_ln_  label="J5_24.243.1_d71695001745"
  LinkPlacement = pos=(150.12,-91.44,0) rot=(0,0,1;1.5708rad)
  LinkedObject = -> Shape002
  Placement = pos=(150.12,-91.44,0) rot=(0,0,1;1.5708rad)
FEATURE [App::Link] C11_GC355DD7LP474KX18K003_3832eaa5f01c_ln_002  label="C10_GC355DD7LP474KX18K003_517d5444c8b2"
  LinkPlacement = pos=(79.121,-81.026,0) rot=(0.57735,0.57735,0.57735;2.0944rad)
  LinkedObject = -> GC355DD7LP474KX18K
  Placement = pos=(79.121,-81.026,0) rot=(0.57735,0.57735,0.57735;2.0944rad)
FEATURE [App::Link] J6_RFPC_SMA27_F005_71e1e65d45ac_ln_001  label="J12_RFPC-SMA27-F005_7e02148dc2e2"
  LinkPlacement = pos=(66.04,-96.52,0) rot=(0.57735,-0.57735,-0.57735;2.0944rad)
  LinkedObject = -> RFPC_SMA27_F
  Placement = pos=(66.04,-96.52,0) rot=(0.57735,-0.57735,-0.57735;2.0944rad)
FEATURE [App::Link] U3_DQ_af74b2632c74_ln_001  label="U1_DQ_aca577252b28"
  LinkPlacement = pos=(99.06,-137.25,8) rot=(0,1,0;3.14159rad)
  LinkedObject = -> DQ
  Placement = pos=(99.06,-137.25,8) rot=(0,1,0;3.14159rad)
FEATURE [App::Link] J3_24_243_1_edf6e0b226a5_ln_001  label="J4_24.243.1_31db098194ed"
  LinkPlacement = pos=(150.12,-104.14,0) rot=(0,0,1;1.5708rad)
  LinkedObject = -> Shape002
  Placement = pos=(150.12,-104.14,0) rot=(0,0,1;1.5708rad)
FEATURE [App::Link] C11_GC355DD7LP474KX18K003_3832eaa5f01c_ln_003  label="C5_GC355DD7LP474KX18K003_493debfcb55a"
  LinkPlacement = pos=(87.63,-110.109,0) rot=(1,0,0;1.5708rad)
  LinkedObject = -> GC355DD7LP474KX18K
  Placement = pos=(87.63,-110.109,0) rot=(1,0,0;1.5708rad)
FEATURE [App::Link] C11_GC355DD7LP474KX18K003_3832eaa5f01c_ln_004  label="C4_GC355DD7LP474KX18K003_4c5ce7d8597c"
  LinkPlacement = pos=(79.121,-114.046,0) rot=(0.57735,0.57735,0.57735;2.0944rad)
  LinkedObject = -> GC355DD7LP474KX18K
  Placement = pos=(79.121,-114.046,0) rot=(0.57735,0.57735,0.57735;2.0944rad)
FEATURE [App::Link] C6_part007_186ecd920058_ln_001  label="C3_part007_4d9b677a6e33"
  LinkPlacement = pos=(102.87,-128.651,0) rot=(0,0,1;3.14159rad)
  LinkedObject = -> part001
  Placement = pos=(102.87,-128.651,0) rot=(0,0,1;3.14159rad)
FEATURE [App::Link] J10_PinHeader_1x03_P254mm_Vertical_3c94ed9524f8_ln_001  label="J13_PinHeader_1x03_P254mm_Vertical_a3efeacecbd7"
  LinkPlacement = pos=(63.5,-104.14,0) rot=(0,0,1;1.5708rad)
  LinkedObject = -> Shape
  Placement = pos=(63.5,-104.14,0) rot=(0,0,1;1.5708rad)
FEATURE [App::Link] C11_GC355DD7LP474KX18K003_3832eaa5f01c_ln_005  label="C8_GC355DD7LP474KX18K003_f604bd3b63a6"
  LinkPlacement = pos=(87.63,-93.599,0) rot=(1,0,0;1.5708rad)
  LinkedObject = -> GC355DD7LP474KX18K
  Placement = pos=(87.63,-93.599,0) rot=(1,0,0;1.5708rad)
FEATURE [App::Link] U3_DQ_af74b2632c74_ln_002  label="U4_DQ_260ab87e0a2d"
  LinkPlacement = pos=(99.06,-87.72,8) rot=(0,1,0;3.14159rad)
  LinkedObject = -> DQ
  Placement = pos=(99.06,-87.72,8) rot=(0,1,0;3.14159rad)
FEATURE [App::Link] J6_RFPC_SMA27_F005_71e1e65d45ac_ln_002  label="J15_RFPC-SMA27-F005_e79da65c2f3f"
  LinkPlacement = pos=(66.04,-78.74,0) rot=(0.57735,-0.57735,-0.57735;2.0944rad)
  LinkedObject = -> RFPC_SMA27_F
  Placement = pos=(66.04,-78.74,0) rot=(0.57735,-0.57735,-0.57735;2.0944rad)
FEATURE [Part::Feature] Shape003  label="J2_PinHeader_1x02_P254mm_Vertical_7797f1f81fd1"
  Placement = pos=(63.5,-68.58,0) rot=(0,0,1;1.5708rad)
  shape: bbox 5.08 x 2.54 x 11.54 mm, 52 faces (baked)
FEATURE [Part::Feature] Shape004  label="J1_PinSocket_1x13_P2.54mm_Vertical_684ecb031951"
  Placement = pos=(88.9,-147.32,0) rot=(0,0,1;1.5708rad)
  shape: bbox 33.02 x 2.54 x 11.6 mm, 348 faces (baked)
FEATURE [App::Link] H2_24929_41eebdcc3b95_ln_001  label="H4_24929_ff52b60ec669"
  LinkPlacement = pos=(125.73,-140.97,-1.5) rot=(1,0,0;1.5708rad)
  LinkedObject = -> Shape001
  Placement = pos=(125.73,-140.97,-1.5) rot=(1,0,0;1.5708rad)
FEATURE [App::Link] J10_PinHeader_1x03_P254mm_Vertical_3c94ed9524f8_ln_002  label="J16_PinHeader_1x03_P254mm_Vertical_890b552459df"
  LinkPlacement = pos=(63.5,-86.36,0) rot=(0,0,1;1.5708rad)
  LinkedObject = -> Shape
  Placement = pos=(63.5,-86.36,0) rot=(0,0,1;1.5708rad)
FEATURE [App::Link] C11_GC355DD7LP474KX18K003_3832eaa5f01c_ln_006  label="C7_GC355DD7LP474KX18K003_95017245eafd"
  LinkPlacement = pos=(79.121,-97.536,0) rot=(0.57735,0.57735,0.57735;2.0944rad)
  LinkedObject = -> GC355DD7LP474KX18K
  Placement = pos=(79.121,-97.536,0) rot=(0.57735,0.57735,0.57735;2.0944rad)
FEATURE [App::Link] C6_part007_186ecd920058_ln_002  label="C9_part007_b16a96295616"
  LinkPlacement = pos=(102.87,-95.631,0) rot=(0,0,1;3.14159rad)
  LinkedObject = -> part001
  Placement = pos=(102.87,-95.631,0) rot=(0,0,1;3.14159rad)
FEATURE [App::Point] Origin027  label="Origin036"
  Role = Origin
FEATURE [Part::Feature] Part__Feature027  label="part007"
  shape: bbox 2.082 x 1.656 x 0.512 mm, 6 faces (baked)
FEATURE [Part::Feature] Part__Feature028  label="part008"
  shape: bbox 0.661 x 1.752 x 0.61 mm, 6 faces (baked)
FEATURE [Part::Feature] Part__Feature029  label="part009"
  shape: bbox 0.661 x 1.752 x 0.61 mm, 6 faces (baked)
FEATURE [App::Part] part002  label="R2_part010_6ae9e8cd3c09"
  Group = -> [Part__Feature027,Part__Feature028,Part__Feature029]
  Origin = -> Origin026
  Placement = pos=(145.288,-75.438,0) rot=(0,0,1;0rad)
FEATURE [App::Link] R2_part010_6ae9e8cd3c09_ln_  label="R1_part010_9a087e8ae435"
  LinkPlacement = pos=(137.922,-75.438,0) rot=(0,0,1;0rad)
  LinkedObject = -> part002
  Placement = pos=(137.922,-75.438,0) rot=(0,0,1;0rad)
FEATURE [App::Part] Top_4ccb
  Group = -> [DQ,U3_DQ_af74b2632c74_ln_,GC355DD7LP474KX18K,Shape,C11_GC355DD7LP474KX18K003_3832eaa5f01c_ln_,part,R4_part003_2be0b62ebf49_ln_,J10_PinHeader_1x03_P254mm_Vertical_3c94ed9524f8_ln_,Shape001,RFPC_SMA27_F,R4_part003_2be0b62ebf49_ln_001,part001,J6_RFPC_SMA27_F005_71e1e65d45ac_ln_,C11_GC355DD7LP474KX18K003_3832eaa5f01c_ln_001,Shape002,C6_part007_186ecd920058_ln_,H2_24929_41eebdcc3b95_ln_,+21 more]
  Origin = -> Origin006
FEATURE [App::Part] Step_Models_4ccb
  Group = -> [Top_4ccb]
  Origin = -> Origin004
FEATURE [App::Part] Board_4ccb  label="HighVoltageBoard"
  Group = -> [Local_CS_4ccb,Board_Geoms_4ccb,Step_Models_4ccb]
  Origin = -> Origin002
  Placement = pos=(-22,76,0) rot=(0,0,1;0rad)
